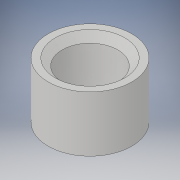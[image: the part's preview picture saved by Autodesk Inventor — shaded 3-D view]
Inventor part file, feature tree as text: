
AUTODESK INVENTOR PART (.ipt)
format: ipt  version: 2018 (Build 220112000, 112)  size: 101,376 bytes
history: native  units: in
note: dims shown in document units (in); Inventor stores cm internally (conversion verified against a paired STEP export)
features: extrude x1, chamfer x1, sketch x1
ambient origin geometry x8: Origin, YZ Plane, XZ Plane, XY Plane, X Axis, Y Axis, Z Axis, Center Point
bodies: Solid1 (feature_tree)
feature tree (3):
  extrude  "Extrusion1"  Depth=1.0in
  chamfer  "Chamfer1"  Distance=1.0in
  sketch  "Sketch3"  dims[d7=1.0in d8=1.5in d9=1.0in d10=0.0in d11=0.125in d12=0.125in d13=45.0deg]
